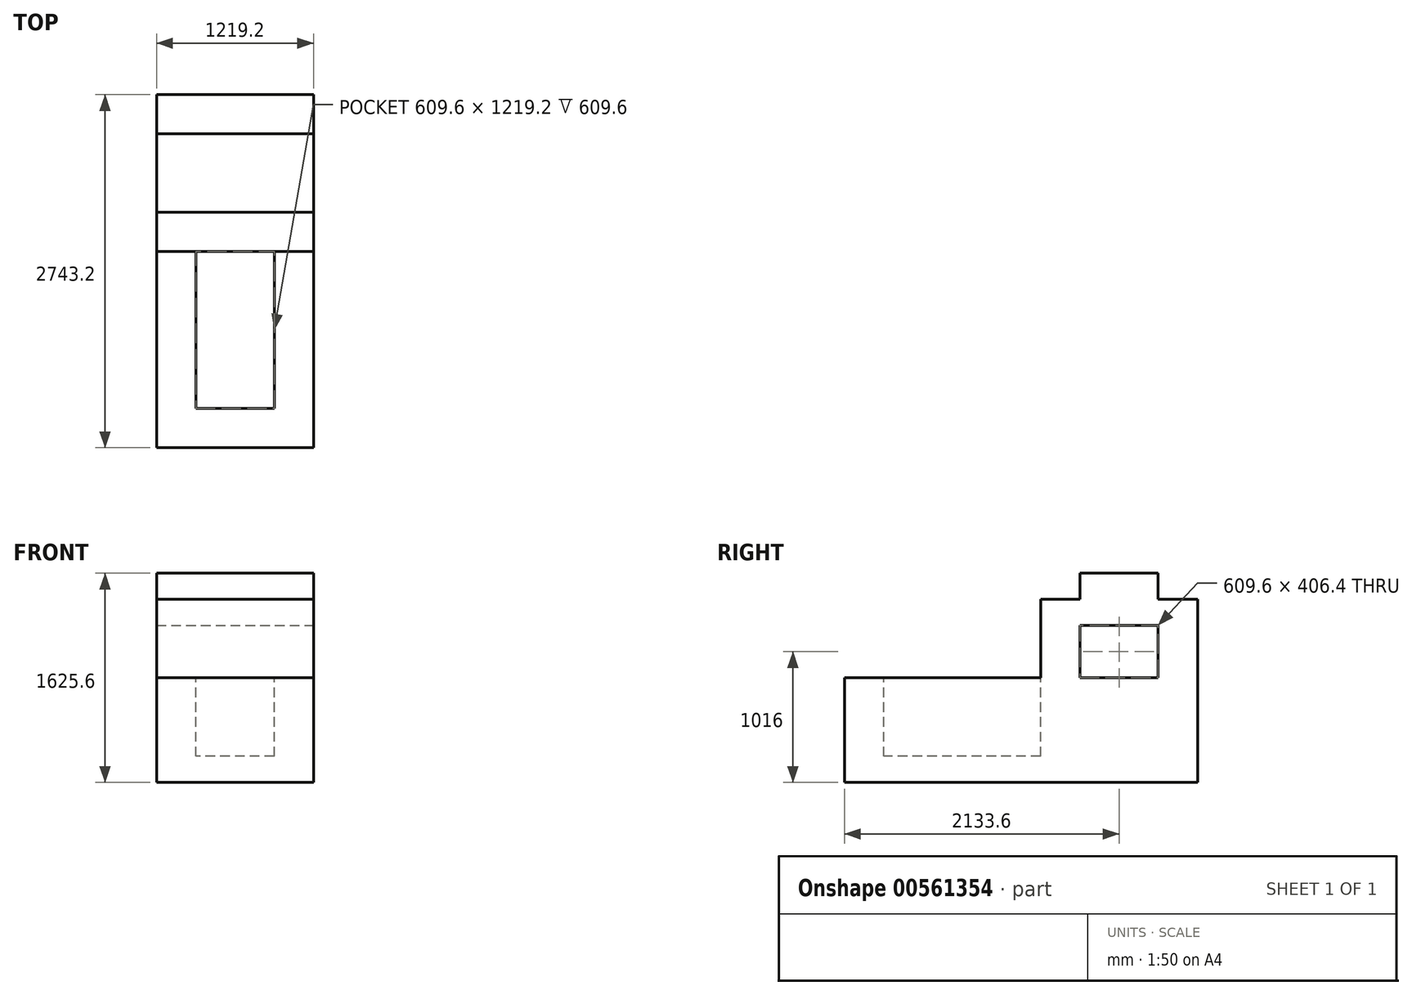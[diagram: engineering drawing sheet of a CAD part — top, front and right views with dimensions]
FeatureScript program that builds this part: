
annotation { "Feature Type Name" : "Feature", "Feature Type Description" : "" }
export const myFeature = defineFeature(function(context is Context, id is Id, definition is map)
    precondition{}
    {
        {
            var Q0;
            Q0=qCreatedBy(makeId("Right.planeOp"),FACE);
            var sketch = newSketch(context, id + "F0", { "sketchPlane" : qUnion([Q0])});
            skLineSegment(sketch, "E0", {"start": v(-1381.46, -975.37) * mm, "end": v(1361.74, -975.37) * mm});
            skLineSegment(sketch, "E1", {"start": v(1361.74, -975.37) * mm, "end": v(1361.74, 447.03) * mm});
            skLineSegment(sketch, "E2", {"start": v(1361.74, 447.03) * mm, "end": v(1056.94, 447.03) * mm});
            skLineSegment(sketch, "E3", {"start": v(1056.94, 447.03) * mm, "end": v(1056.94, 650.23) * mm});
            skLineSegment(sketch, "E4", {"start": v(1056.94, 650.23) * mm, "end": v(447.34, 650.23) * mm});
            skLineSegment(sketch, "E5", {"start": v(447.34, 650.23) * mm, "end": v(447.34, 447.03) * mm});
            skLineSegment(sketch, "E6", {"start": v(447.34, 447.03) * mm, "end": v(142.54, 447.03) * mm});
            skLineSegment(sketch, "E7", {"start": v(142.54, 447.03) * mm, "end": v(142.54, -162.57) * mm});
            skLineSegment(sketch, "E8", {"start": v(142.54, -162.57) * mm, "end": v(-1381.46, -162.57) * mm});
            skLineSegment(sketch, "E9", {"start": v(-1381.46, -162.57) * mm, "end": v(-1381.46, -975.37) * mm});
            skSolve(sketch);
        }
        {
            var Q0;
            Q0 = qSketchRegion(id + "F0", true);
            extrude(context, id + "F1", {"entities" : qUnion([Q0]), "depth" : 1219.2 * mm, "offsetDistance" : 25.4 * mm});
        }
        {
            var Q0;
            Q0=makeQuery(id+"F1.opExtrude","SWEPT_FACE",FACE,{"disambiguationData":[OSD([sQuery(id+"F0.wireOp",EDGE,"E8")])]});
            var sketch = newSketch(context, id + "F2", { "sketchPlane" : qUnion([Q0])});
            skLineSegment(sketch, "E10", {"start": v(304.8, 142.54) * mm, "end": v(304.8, -1076.66) * mm});
            skLineSegment(sketch, "E11", {"start": v(304.8, -1076.66) * mm, "end": v(914.4, -1076.66) * mm});
            skLineSegment(sketch, "E12", {"start": v(914.4, -1076.66) * mm, "end": v(914.4, 142.54) * mm});
            skLineSegment(sketch, "E13", {"start": v(304.8, 142.54) * mm, "end": v(914.4, 142.54) * mm});
            skSolve(sketch);
        }
        {
            var Q0;
            Q0=makeQuery(id+"F2.imprint","IMPRINT",FACE,{"disambiguationData":[TD([[makeQuery(id+"F2.imprint","IMPRINT",EDGE,{"derivedFrom":sQuery(id+"F2.wireOp",EDGE,"E10")}),1.0]])]});
            extrude(context, id + "F3", {"entities" : qUnion([Q0]), "operationType" : NewBodyOperationType.REMOVE, "oppositeDirection" : true, "depth" : 609.6 * mm, "offsetDistance" : 25.4 * mm});
        }
        {
            var Q0;
            Q0=makeQuery(id+"F1.opExtrude","CAP_FACE",FACE,{"disambiguationData":[OSD([sQuery(id+"F0.wireOp",EDGE,"E0"),sQuery(id+"F0.wireOp",EDGE,"E1"),sQuery(id+"F0.wireOp",EDGE,"E2"),sQuery(id+"F0.wireOp",EDGE,"E3"),sQuery(id+"F0.wireOp",EDGE,"E4"),sQuery(id+"F0.wireOp",EDGE,"E5"),sQuery(id+"F0.wireOp",EDGE,"E6"),sQuery(id+"F0.wireOp",EDGE,"E7"),sQuery(id+"F0.wireOp",EDGE,"E8"),sQuery(id+"F0.wireOp",EDGE,"E9")])],"isStart":false});
            var sketch = newSketch(context, id + "F4", { "sketchPlane" : qUnion([Q0])});
            skLineSegment(sketch, "E14", {"start": v(1056.94, 243.83) * mm, "end": v(1056.94, -162.57) * mm});
            skLineSegment(sketch, "E15", {"start": v(1056.94, -162.57) * mm, "end": v(447.34, -162.57) * mm});
            skLineSegment(sketch, "E16", {"start": v(1056.94, 243.83) * mm, "end": v(447.34, 243.83) * mm});
            skLineSegment(sketch, "E17", {"start": v(447.34, 243.83) * mm, "end": v(447.34, -162.57) * mm});
            skSolve(sketch);
        }
        {
            var Q0;
            Q0 = qSketchRegion(id + "F4", true);
            extrude(context, id + "F5", {"entities" : qUnion([Q0]), "operationType" : NewBodyOperationType.REMOVE, "endBound" : BoundingType.THROUGH_ALL, "oppositeDirection" : true, "depth" : 25.4 * mm, "offsetDistance" : 25.4 * mm});
        }
    });
